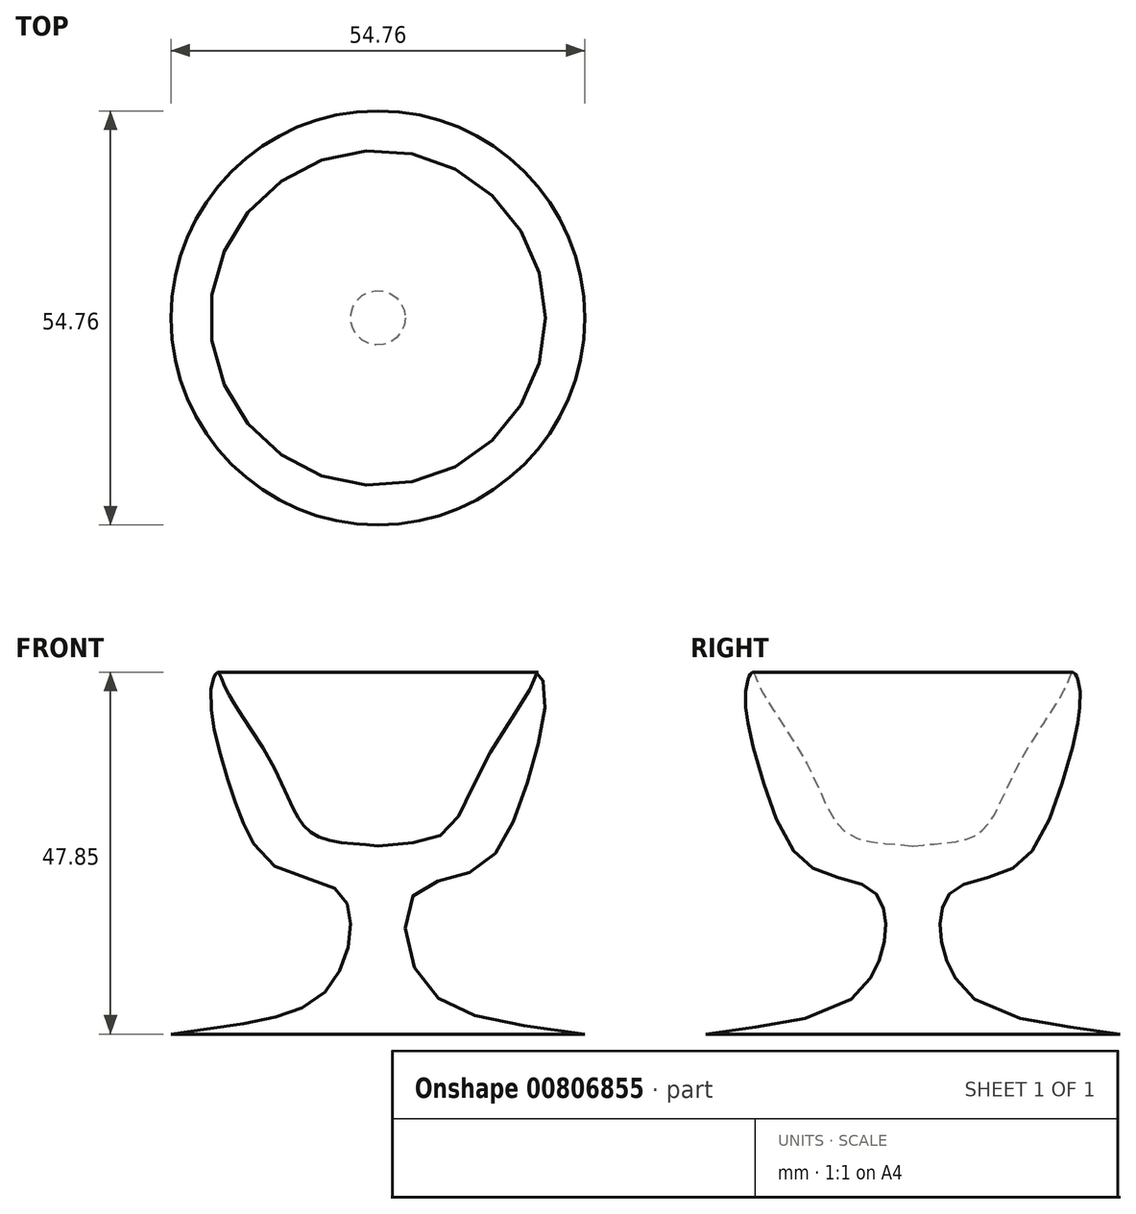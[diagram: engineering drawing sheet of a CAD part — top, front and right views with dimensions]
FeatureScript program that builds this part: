
annotation { "Feature Type Name" : "Feature", "Feature Type Description" : "" }
export const myFeature = defineFeature(function(context is Context, id is Id, definition is map)
    precondition{}
    {
        {
            var Q0;
            Q0=qCreatedBy(makeId("Front.planeOp"),FACE);
            var sketch = newSketch(context, id + "F0", { "sketchPlane" : qUnion([Q0])});
            skFitSpline(sketch, "E0", {"points": [v(27.38, 0) * mm, v(6.26, 6.44) * mm, v(4.74, 18.41) * mm, v(13.22, 21.9) * mm, v(19.55, 32.64) * mm, v(22.11, 45.4) * mm, v(21.2, 47.85) * mm, v(20.31, 46.05) * mm, v(13.7, 35.15) * mm, v(8.92, 26.69) * mm, v(0, 24.87) * mm], "startDerivative": vector(-202.98, 30.7) * mm, "endDerivative": vector(-117.48, -13.86) * mm});
            skLineSegment(sketch, "E1", {"start": v(0, 24.87) * mm, "end": v(0, 0) * mm});
            skLineSegment(sketch, "E2", {"start": v(0, 0) * mm, "end": v(27.38, 0) * mm});
            skSolve(sketch);
        }
        {
            var Q0;
            Q0=makeQuery(id+"F0.imprint","IMPRINT",FACE,{"disambiguationData":[TD([[makeQuery(id+"F0.imprint","IMPRINT",EDGE,{"derivedFrom":sQuery(id+"F0.wireOp",EDGE,"E0")}),1.0]])]});
            var Q1;
            Q1=sQuery(id+"F0.wireOp",EDGE,"E1");
            revolve(context, id + "F1", {"surfaceOperationType" : NewSurfaceOperationType.NEW, "entities" : qUnion([Q0]), "axis" : qUnion([Q1]), "revolveType" : RevolveType.FULL});
        }
    });
